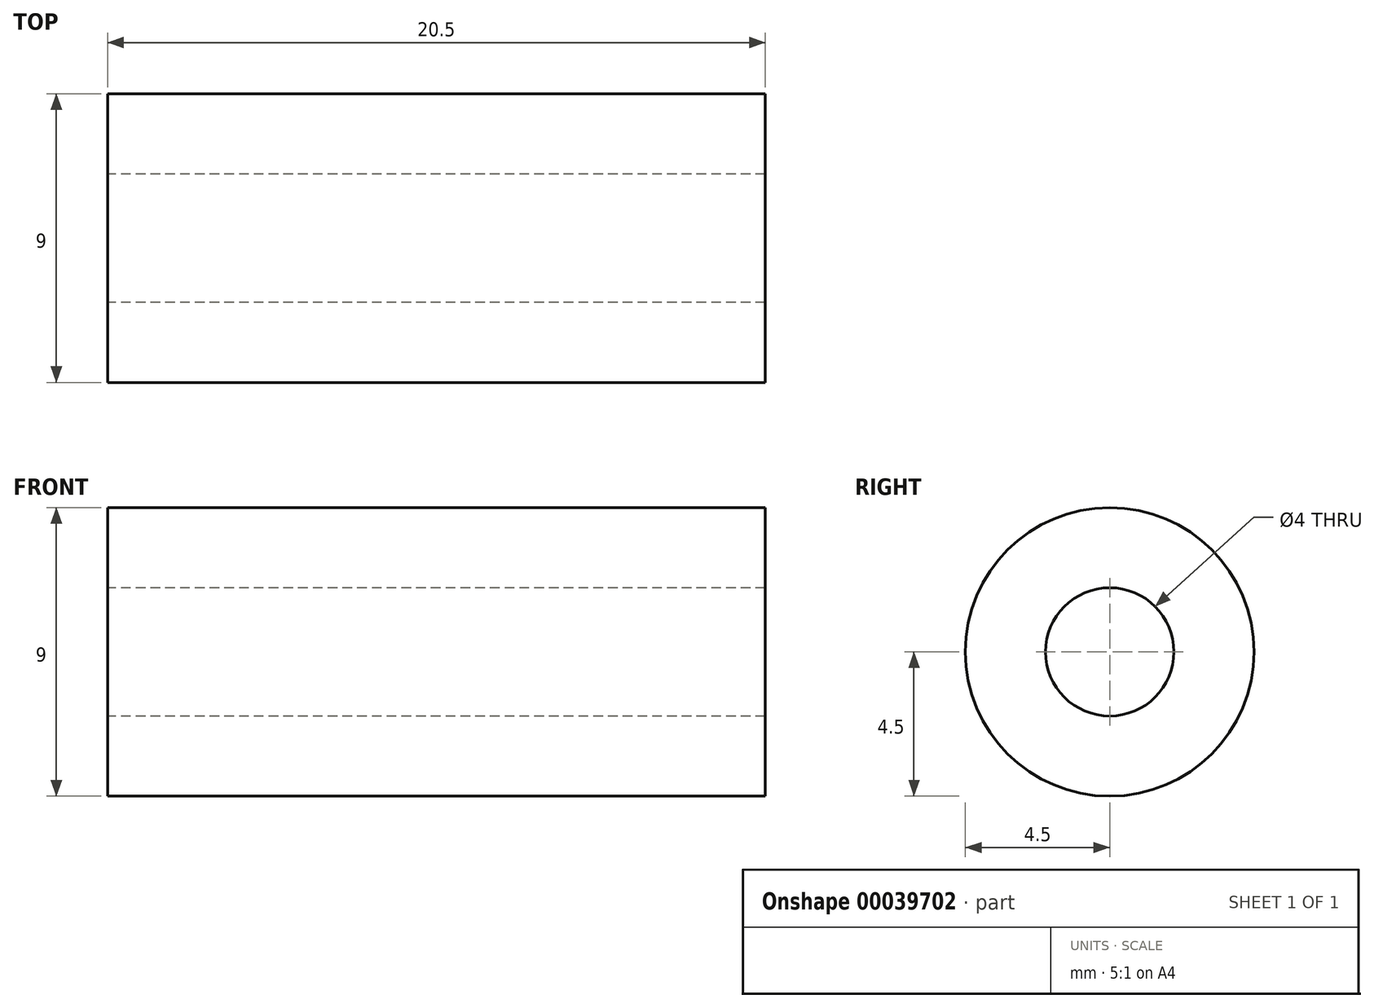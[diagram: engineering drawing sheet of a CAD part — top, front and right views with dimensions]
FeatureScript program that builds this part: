
annotation { "Feature Type Name" : "Feature", "Feature Type Description" : "" }
export const myFeature = defineFeature(function(context is Context, id is Id, definition is map)
    precondition{}
    {
        {
            var Q0;
            Q0=qCreatedBy(makeId("Right.planeOp"),FACE);
            var sketch = newSketch(context, id + "F0", { "sketchPlane" : qUnion([Q0])});
            skCircle(sketch, "E0", {"center": v(0, 0) * mm, "radius": 4.5 * mm});
            skCircle(sketch, "E1", {"center": v(0, 0) * mm, "radius": 2 * mm});
            skSolve(sketch);
        }
        {
            var Q0;
            Q0=makeQuery(id+"F0.imprint","IMPRINT",FACE,{"disambiguationData":[TD([[makeQuery(id+"F0.imprint","IMPRINT",EDGE,{"derivedFrom":sQuery(id+"F0.wireOp",EDGE,"E0")}),1.0]])]});
            extrude(context, id + "F1", {"entities" : qUnion([Q0]), "depth" : 20.5 * mm});
        }
    });
